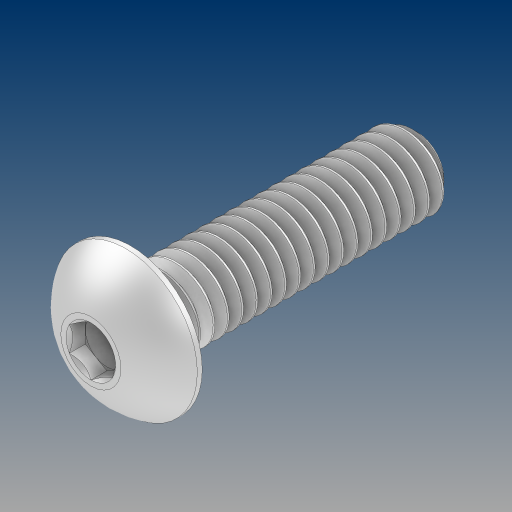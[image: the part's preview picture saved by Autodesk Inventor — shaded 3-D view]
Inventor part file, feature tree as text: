
AUTODESK INVENTOR PART (.ipt)
format: ipt  version: 2024.3 (Build 283343000, 343)  size: 584,192 bytes
history: native  units: in
note: dims shown in document units (in); Inventor stores cm internally (conversion verified against a paired STEP export)
features: revolve x1
ambient origin geometry x8: Origin, YZ Plane, XZ Plane, XY Plane, X Axis, Y Axis, Z Axis, Center Point
bodies: Solid1 (feature_tree)
feature tree (1):
  revolve  "Revolve2"  [1 undecoded]
note: 1 required parameter value undecoded (feature->parameter linkage not recoverable at this tier; creation-order binding heuristic only, values carry confidence <= 0.55)
